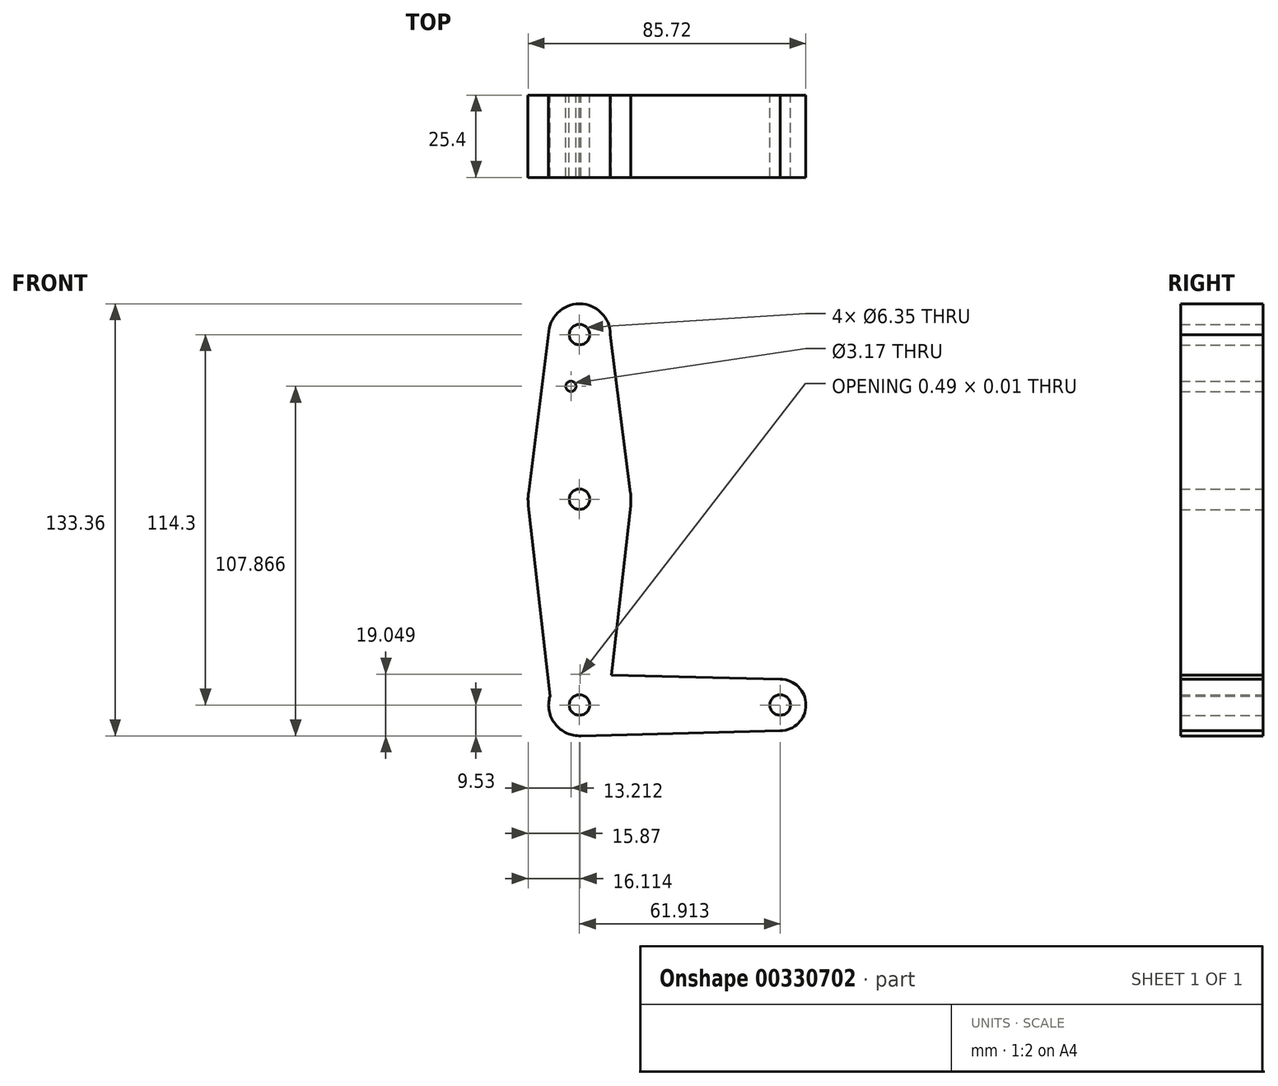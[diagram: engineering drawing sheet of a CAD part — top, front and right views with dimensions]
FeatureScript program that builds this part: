
annotation { "Feature Type Name" : "Feature", "Feature Type Description" : "" }
export const myFeature = defineFeature(function(context is Context, id is Id, definition is map)
    precondition{}
    {
        {
            var Q0;
            Q0=qCreatedBy(makeId("Front.planeOp"),FACE);
            var sketch = newSketch(context, id + "F0", { "sketchPlane" : qUnion([Q0])});
            skLineSegment(sketch, "E0", {"start": v(0, 0) * mm, "end": v(0, 114.3) * mm, "construction": true});
            skLineSegment(sketch, "E1", {"start": v(0, 0) * mm, "end": v(61.91, 0) * mm, "construction": true});
            skCircle(sketch, "E2", {"center": v(0, 114.3) * mm, "radius": 9.53 * mm});
            skCircle(sketch, "E3", {"center": v(0, 63.5) * mm, "radius": 15.88 * mm});
            skCircle(sketch, "E4", {"center": v(0, 0) * mm, "radius": 9.53 * mm});
            skCircle(sketch, "E5", {"center": v(61.91, 0) * mm, "radius": 7.94 * mm});
            skLineSegment(sketch, "E6", {"start": v(-9.52, 114.3) * mm, "end": v(-15.75, 65.5) * mm});
            skLineSegment(sketch, "E7", {"start": v(9.52, 114.3) * mm, "end": v(16, 63.5) * mm});
            skLineSegment(sketch, "E8", {"start": v(15.76, 61.6) * mm, "end": v(9.13, 2.7) * mm});
            skLineSegment(sketch, "E9", {"start": v(-15.76, 61.6) * mm, "end": v(-9.13, 2.7) * mm});
            skLineSegment(sketch, "E10", {"start": v(0, 9.53) * mm, "end": v(61.91, 7.94) * mm});
            skLineSegment(sketch, "E11", {"start": v(61.91, -7.94) * mm, "end": v(0, -9.53) * mm});
            skCircle(sketch, "E12", {"center": v(0, 114.3) * mm, "radius": 3.18 * mm});
            skCircle(sketch, "E13", {"center": v(0, 63.5) * mm, "radius": 3.18 * mm});
            skCircle(sketch, "E14", {"center": v(0, 0) * mm, "radius": 3.18 * mm});
            skCircle(sketch, "E15", {"center": v(61.91, 0) * mm, "radius": 3.18 * mm});
            skCircle(sketch, "E16", {"center": v(-2.66, 98.34) * mm, "radius": 1.59 * mm});
            skSolve(sketch);
        }
        {
            var Q0;
            Q0 = qSketchRegion(id + "F0", true);
            extrude(context, id + "F1", {"entities" : qUnion([Q0]), "depth" : 25.4 * mm});
        }
    });
